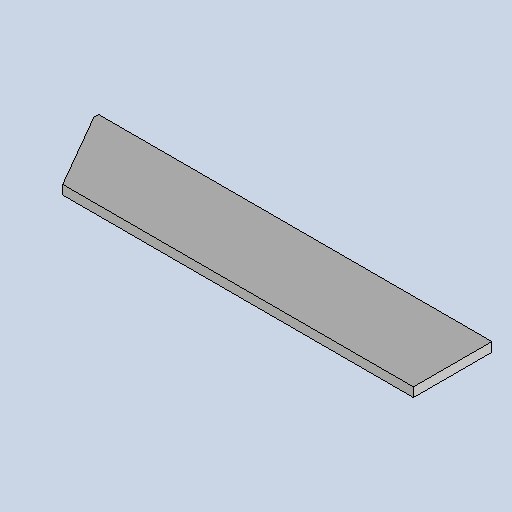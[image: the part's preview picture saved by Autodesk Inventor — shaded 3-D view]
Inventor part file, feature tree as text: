
AUTODESK INVENTOR PART (.ipt)
format: ipt  version: 2025 (Build 290162010, 162A)  size: 164,352 bytes
history: native  units: mm
features: other x2, sheet_metal_op x1, sketch x1
ambient origin geometry x8: Origin, YZ Plane, XZ Plane, XY Plane, X Axis, Y Axis, Z Axis, Center Point
bodies: Body1 (feature_tree)
feature tree (4):
  sheet_metal_op  "Face1"
  sketch  "Sketch1"  dims[d16=10.0mm d17=85.0mm d18=426.0mm d19=60.0deg d20=5.0mm]
  other  "Plate1"
  other  "Definition1"
